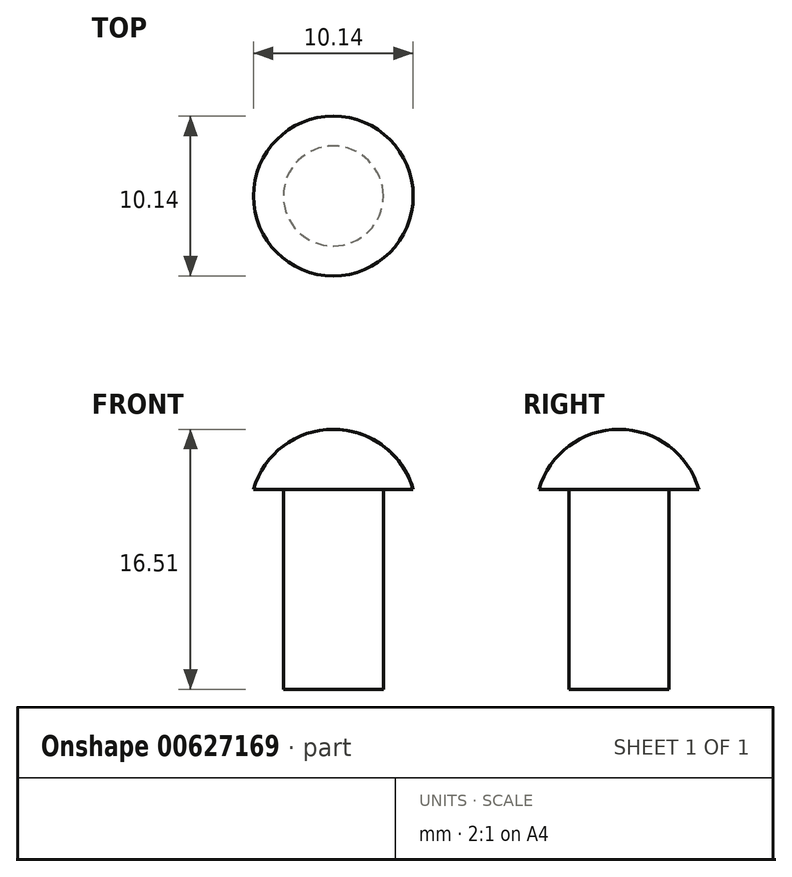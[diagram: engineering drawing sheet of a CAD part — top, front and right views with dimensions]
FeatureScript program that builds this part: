
annotation { "Feature Type Name" : "Feature", "Feature Type Description" : "" }
export const myFeature = defineFeature(function(context is Context, id is Id, definition is map)
    precondition{}
    {
        {
            var Q0;
            Q0=qCreatedBy(makeId("Front.planeOp"),FACE);
            var sketch = newSketch(context, id + "F0", { "sketchPlane" : qUnion([Q0])});
            skLineSegment(sketch, "E0", {"start": v(0, 0) * mm, "end": v(3.18, 0) * mm});
            skLineSegment(sketch, "E1", {"start": v(3.18, 0) * mm, "end": v(3.18, 12.7) * mm});
            skLineSegment(sketch, "E2", {"start": v(0, 0) * mm, "end": v(0, 16.51) * mm});
            skLineSegment(sketch, "E3", {"start": v(0, 16.51) * mm, "end": v(0, 11.23) * mm});
            skArc(sketch, "E4", {"start": v(0, 16.51) * mm, "mid": v(3.17, 15.45) * mm, "end": v(5.07, 12.7) * mm});
            skLineSegment(sketch, "E5", {"start": v(3.18, 12.7) * mm, "end": v(5.07, 12.7) * mm});
            skSolve(sketch);
        }
        {
            var Q0;
            Q0=makeQuery(id+"F0.imprint","IMPRINT",FACE,{"disambiguationData":[TD([[makeQuery(id+"F0.imprint","IMPRINT",EDGE,{"derivedFrom":sQuery(id+"F0.wireOp",EDGE,"E0")}),1.0]])]});
            var Q1;
            Q1=sQuery(id+"F0.wireOp",EDGE,"E2");
            revolve(context, id + "F1", {"entities" : qUnion([Q0]), "axis" : qUnion([Q1]), "revolveType" : RevolveType.FULL});
        }
    });
